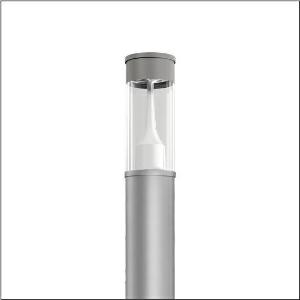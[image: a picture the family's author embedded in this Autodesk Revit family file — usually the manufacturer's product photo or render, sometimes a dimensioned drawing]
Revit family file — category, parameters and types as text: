
# Revit family: city-light_260_iq___pl1_2s_5xa5295of14h_8957
name_source: partatom
category: Lighting Fixtures
units: mm (PartAtom-declared; Revit-internal decimal feet)

## family parameters
Cut with Voids When Loaded = No
Host = Face
Light Source = No
Part Type = Normal
Room Calculation Point = No
Round Connector Dimension = Use Diameter
Shared = No

## types (1)
- --- (1 x LED, 2970 lm, 21.8 W, 2700K)
    Apparent Load = 22 VA
    CIE Flux Codes = 23 62 94 96 100
    Color Rendering = 70
    Color Temperature = 2700K
    Default Elevation = 1800 mm
    Description = City-Light 260 iQ, light pillar, Module 540 iQ-SR, primary light control with 3 zone facetted reflector, of plastic, silver coated, highly specular, structured, primary optical cover: cover, of PMMA, transparent, partly coated, light distribution: PL1.2s, primary light characteristic: symmetric, LED, High Power LED, rated luminous flux: 2.970lm, luminous efficacy: 136lm/W, light colour: 727, colour temperature: 2700K, control gear: ECG iQ, control: presetting dimming logarithmic, Street-Remote, Auto-Match, Temp-Guard, Lumen-Switch, Night-Set, Smart-Wire, Light-Fading, Desk-Remote (wireless, voltage-free reading and setting of iQ features in the workshop via application-optimized NFC function/RFID function), optimised constant luminous flux control (CLO 2.0), with terminal, 6-pole, max. 2.5mm², mains connection: 230..240V, AC, 50/60Hz, start of lifetime: 22W, end of service life: 23W, reduction: 11W, luminaire housing, cylindrical, of extruded aluminium section, coated, Siteco® metallic grey (DB 702S), length: 2.600mm, diameter: 200mm, Module 540 iQ-SR, traffic white (RAL 9016), equipment: standard, protection rating (complete): IP65, insulation class (complete): insulation class II (safety insulation), certification: CE, ENEC, VDE, packaging unit: 1 piece

Light Distribution: PL1.2s
    Height = 500 mm
    Lamp = 1 x LED
    Lamp Light Flux = 2970 lm
    Lamp Power = 21.8 W
    Lamp count = 1
    Length = 200 mm  [stored 0.656168 ft]
    Luminous efficacy = 136 lm/W
    Manufacturer = Siteco
    ModVariant = No
    Model = 5XA5295OF14H
    Mounting Place = Floor
    Mounting Type = Freestanding
    Number of Poles = 1
    OnlyDefault = Yes
    Power Factor = 1
    Product Name = City-Light 260 iQ | PL1.2s
    Product group = light pillar
    ProductGroupID = 1303
    Protection Class = Protection class II
    Protection Degree = IP 65
    RLX_Detail_Level = 1
    RLX_Emergency_Light_Flux = 0 lm
    RLX_Emergency_Type = 0
    RLX_Emergency_Type_DB = No
    RlxData = <blob elided: 28765 chars, md5=af072368>
    Socket = socket
    Standby Power = 0 W
    System Light Flux = 2970 lm
    System Power = 22 W
    Type Comments = factory setting: luminous flux: 100 % | dim-lin: 254 | 456 mA
    Type Image = l_1006920.jpg
    URL = http://relux.com
    VarID = @adj_094433
    Voltage = 0 V
    Weight = 0.00 kg
    Width = 0 mm  [stored 0 ft]

note: [stored X ft] marks values corroborated as IEEE doubles in the binary element streams (Revit-internal decimal feet)

## geometry (parser evidence)
native form markers: Blend x4, Sweep x10
no freeform markers — native parametric forms only
